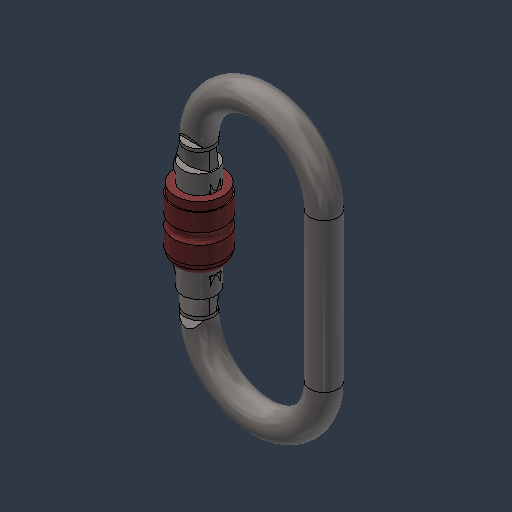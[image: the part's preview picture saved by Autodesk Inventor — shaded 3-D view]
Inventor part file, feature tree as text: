
AUTODESK INVENTOR PART (.ipt)
format: ipt  version: 2024.3 (Build 283343000, 343)  size: 254,464 bytes
history: native  units: mm (DEFAULTED — no unit token found)
features: fillet x1
ambient origin geometry x8: Origin, YZ Plane, XZ Plane, XY Plane, X Axis, Y Axis, Z Axis, Center Point
bodies: Solid1 (feature_tree)
feature tree (1):
  fillet  "Fillet6"  [1 undecoded]
note: 1 required parameter value undecoded (feature->parameter linkage not recoverable at this tier; creation-order binding heuristic only, values carry confidence <= 0.55)
